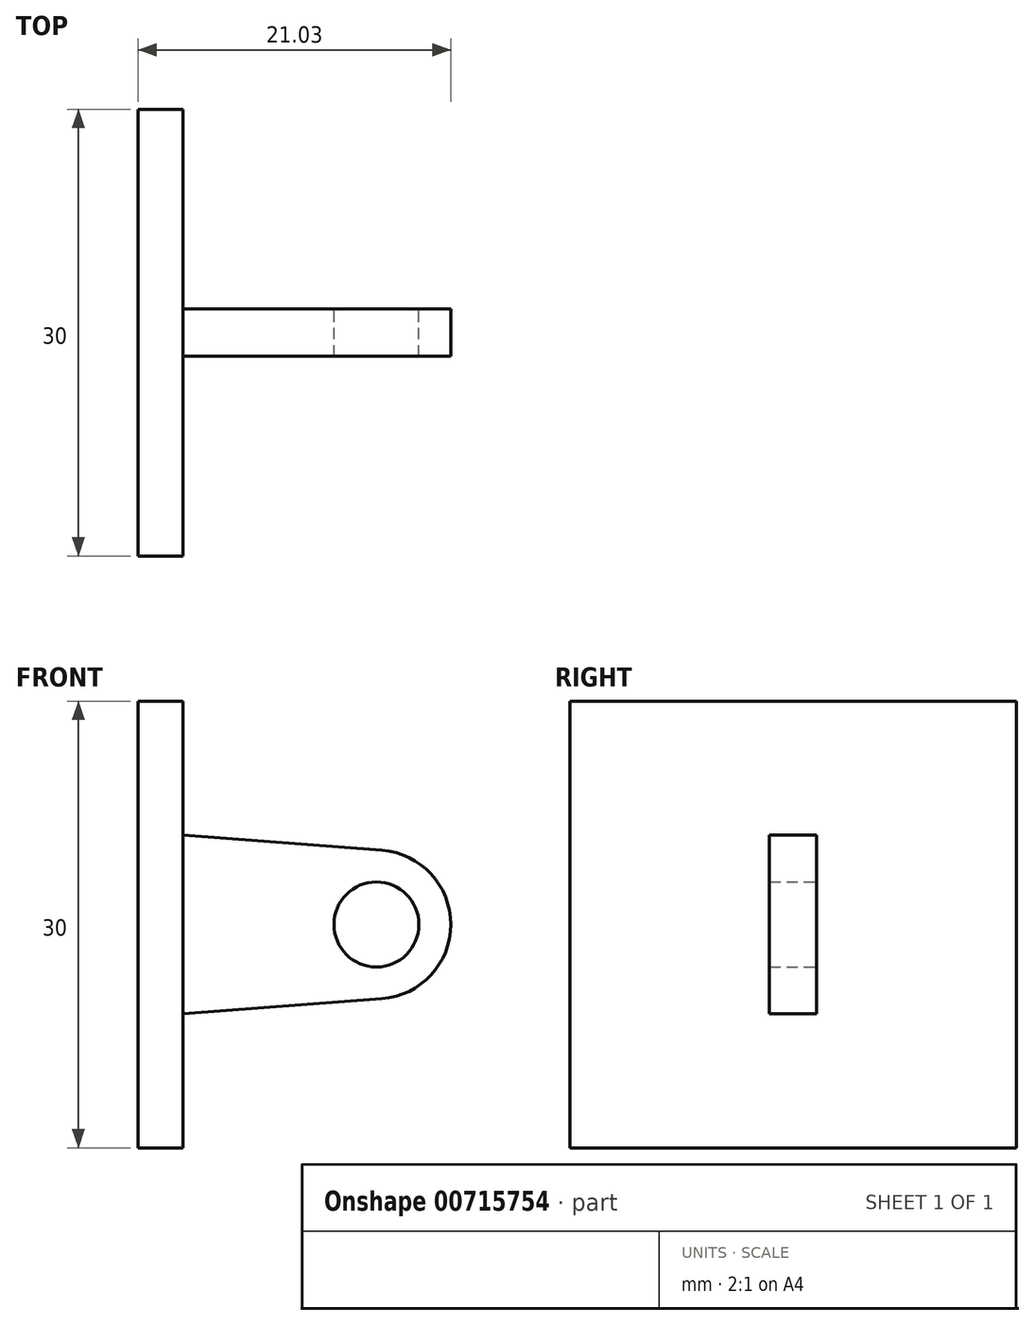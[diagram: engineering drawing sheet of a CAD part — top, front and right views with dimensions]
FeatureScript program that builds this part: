
annotation { "Feature Type Name" : "Feature", "Feature Type Description" : "" }
export const myFeature = defineFeature(function(context is Context, id is Id, definition is map)
    precondition{}
    {
        {
            var Q0;
            Q0=qCreatedBy(makeId("Front.planeOp"),FACE);
            var sketch = newSketch(context, id + "F0", { "sketchPlane" : qUnion([Q0])});
            skCircle(sketch, "E0", {"center": v(0, 0) * mm, "radius": 2.85 * mm});
            skCircle(sketch, "E1", {"center": v(0, 0) * mm, "radius": 5 * mm, "construction": true});
            skLineSegment(sketch, "E2", {"start": v(-13, 6) * mm, "end": v(-13, -6) * mm});
            skLineSegment(sketch, "E3", {"start": v(-13, -6) * mm, "end": v(0.38, -4.99) * mm});
            skLineSegment(sketch, "E4", {"start": v(-13, 6) * mm, "end": v(0.38, 4.99) * mm});
            skArc(sketch, "E5", {"start": v(0.38, 4.99) * mm, "mid": v(5, 0) * mm, "end": v(0.38, -4.99) * mm});
            skSolve(sketch);
        }
        {
            var Q0;
            Q0 = qSketchRegion(id + "F0", true);
            extrude(context, id + "F1", {"entities" : qUnion([Q0]), "depth" : 3.17 * mm, "offsetDistance" : 25 * mm, "symmetric" : true});
        }
        {
            var Q0;
            Q0=makeQuery(id+"F1.opExtrude","SWEPT_FACE",FACE,{"disambiguationData":[OSD([sQuery(id+"F0.wireOp",EDGE,"E2")])]});
            var sketch = newSketch(context, id + "F2", { "sketchPlane" : qUnion([Q0])});
            skLineSegment(sketch, "E6.bottom", {"start": v(-15, -15) * mm, "end": v(15, -15) * mm});
            skLineSegment(sketch, "E6.top", {"start": v(-15, 15) * mm, "end": v(15, 15) * mm});
            skLineSegment(sketch, "E6.left", {"start": v(-15, -15) * mm, "end": v(-15, 15) * mm});
            skLineSegment(sketch, "E6.right", {"start": v(15, -15) * mm, "end": v(15, 15) * mm});
            skSolve(sketch);
        }
        {
            var Q0;
            Q0 = qSketchRegion(id + "F2", true);
            extrude(context, id + "F3", {"entities" : qUnion([Q0]), "operationType" : NewBodyOperationType.ADD, "depth" : (3.17 - 0.15) * mm, "offsetDistance" : 25 * mm});
        }
    });
